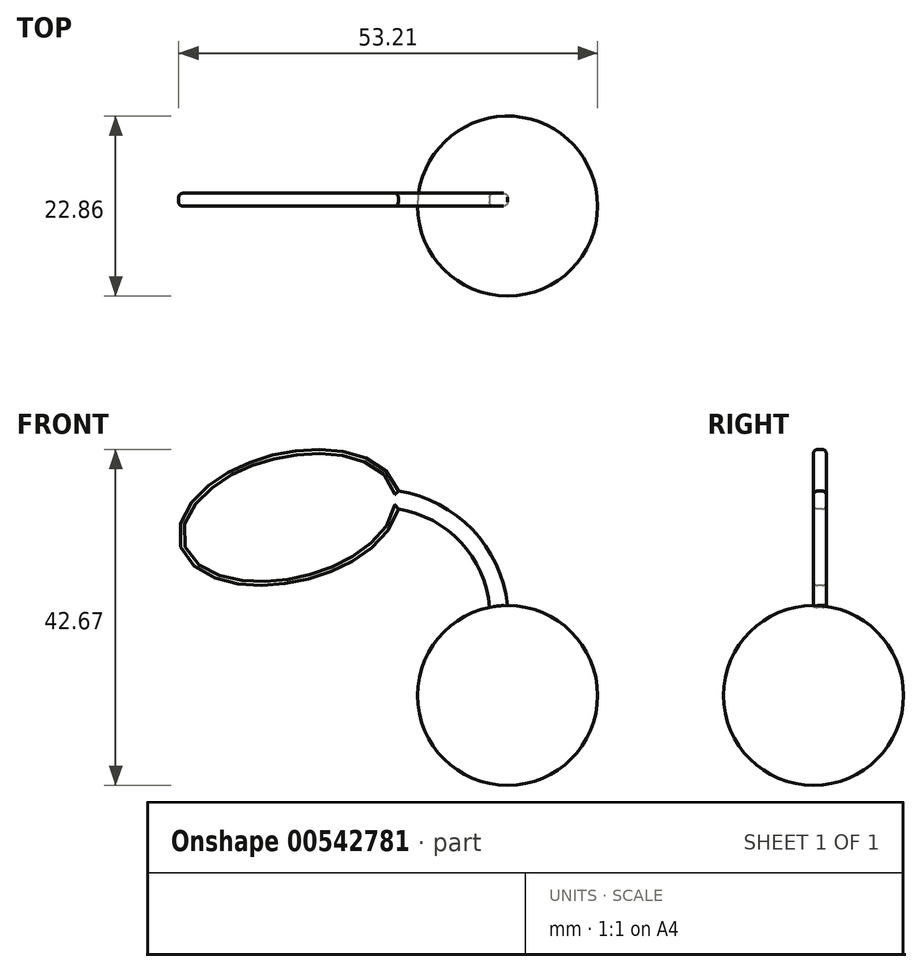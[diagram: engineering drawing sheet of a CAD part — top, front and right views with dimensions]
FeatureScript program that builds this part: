
annotation { "Feature Type Name" : "Feature", "Feature Type Description" : "" }
export const myFeature = defineFeature(function(context is Context, id is Id, definition is map)
    precondition{}
    {
        {
            var Q0;
            Q0=qCreatedBy(makeId("Front.planeOp"),FACE);
            var sketch = newSketch(context, id + "F0", { "sketchPlane" : qUnion([Q0])});
            skCircle(sketch, "E0", {"center": v(0, 39.89) * mm, "radius": 11.43 * mm});
            skPoint(sketch, "E1.center.orphan", {"position": v(0, 51.32) * mm});
            skArc(sketch, "E2", {"start": v(0, 51.32) * mm, "mid": v(-4.47, 60.95) * mm, "end": v(-13.89, 65.85) * mm});
            skEllipticalArc(sketch, "E3", {});
            skArc(sketch, "E4", {"start": v(-2.29, 51.09) * mm, "mid": v(-5.92, 59.33) * mm, "end": v(-13.89, 63.56) * mm});
            skLineSegment(sketch, "E5", {"start": v(-11.43, 39.89) * mm, "end": v(11.43, 39.89) * mm});
            const initialGuessF0  = {"E3": [-0.02776575009105331, 0.06250017627483125, 0.972096228515868, 0.23458244287504867, 0.014278696427545014, 0.008185501633882855, 0, 6.008253334236654]};
            skSetInitialGuess(sketch, initialGuessF0);
            skSolve(sketch);
        }
        {
            var Q0;
            {var subQ2=sQuery(id+"F0.wireOp",EDGE,"E5");Q0=makeQuery(id+"F0.imprint","IMPRINT",FACE,{"disambiguationData":[TD([[makeQuery(id+"F0.imprint","IMPRINT",EDGE,{"derivedFrom":subQ2}),1.0]])]});}
            var Q1;
            Q1=sQuery(id+"F0.wireOp",EDGE,"E5");
            revolve(context, id + "F1", {"entities" : qUnion([Q0]), "axis" : qUnion([Q1]), "revolveType" : RevolveType.FULL});
        }
        {
            var Q0;
            {var subQ0=sQuery(id+"F0.wireOp",EDGE,"e57f1007-ea98-437a-b2c9-17ab534581e4");Q0=makeQuery(id+"F0.imprint","IMPRINT",FACE,{"disambiguationData":[TD([[makeQuery(id+"F0.imprint","IMPRINT",EDGE,{"derivedFrom":subQ0}),1.0]])]});}
            var Q1;
            {var subQ0=sQuery(id+"F0.wireOp",EDGE,"E2");Q1=makeQuery(id+"F0.imprint","IMPRINT",FACE,{"disambiguationData":[TD([[makeQuery(id+"F0.imprint","IMPRINT",EDGE,{"derivedFrom":subQ0}),1.0]])]});}
            extrude(context, id + "F2", {"entities" : qUnion([Q0, Q1]), "oppositeDirection" : true, "depth" : 1.62 * mm, "offsetDistance" : 25.4 * mm});
        }
        {
            var Q0;
            {var subQ0=sQuery(id+"F0.wireOp",EDGE,"e57f1007-ea98-437a-b2c9-17ab534581e4");var subQ1=sQuery(id+"F0.wireOp",EDGE,"E3");Q0=makeQuery(id+"F2.opExtrude","CAP_EDGE",EDGE,{"disambiguationData":[OSD([subQ1]),TDD([makeQuery(id+"F0.imprint","IMPRINT",EDGE,{"disambiguationData":[TD([[makeQuery(id+"F0.imprint","INTERSECT",VERTEX,{"derivedFrom":[sQuery(id+"F0.wireOp",EDGE,"E2"),subQ1,subQ0]}),-1.0]])],"derivedFrom":subQ1})])],"isStart":true});}
            var Q1;
            {var subQ0=sQuery(id+"F0.wireOp",EDGE,"e57f1007-ea98-437a-b2c9-17ab534581e4");var subQ1=sQuery(id+"F0.wireOp",EDGE,"E3");Q1=makeQuery(id+"F2.opExtrude","CAP_EDGE",EDGE,{"disambiguationData":[OSD([subQ1]),TDD([makeQuery(id+"F0.imprint","IMPRINT",EDGE,{"disambiguationData":[TD([[makeQuery(id+"F0.imprint","INTERSECT",VERTEX,{"derivedFrom":[sQuery(id+"F0.wireOp",EDGE,"E2"),subQ1,subQ0]}),-1.0]])],"derivedFrom":subQ1})])],"isStart":false});}
            fillet(context, id + "F3", {"entities" : qUnion([Q0, Q1]), "radius" : 0.5 * mm, "tangentPropagation" : true, "allowEdgeOverflow" : false});
        }
        {
            var Q0;
            Q0=makeQuery(id+"F2.opExtrude","CAP_EDGE",EDGE,{"disambiguationData":[OSD([sQuery(id+"F0.wireOp",EDGE,"E2")])],"isStart":true});
            var Q1;
            Q1=makeQuery(id+"F2.opExtrude","CAP_EDGE",EDGE,{"disambiguationData":[OSD([sQuery(id+"F0.wireOp",EDGE,"E2")])],"isStart":false});
            var Q2;
            Q2=makeQuery(id+"F2.opExtrude","CAP_EDGE",EDGE,{"disambiguationData":[OSD([sQuery(id+"F0.wireOp",EDGE,"E4")])],"isStart":true});
            var Q3;
            Q3=makeQuery(id+"F2.opExtrude","CAP_EDGE",EDGE,{"disambiguationData":[OSD([sQuery(id+"F0.wireOp",EDGE,"E4")])],"isStart":false});
            fillet(context, id + "F4", {"entities" : qUnion([Q0, Q1, Q2, Q3]), "radius" : 0.5 * mm, "tangentPropagation" : true, "allowEdgeOverflow" : false});
        }
    });
